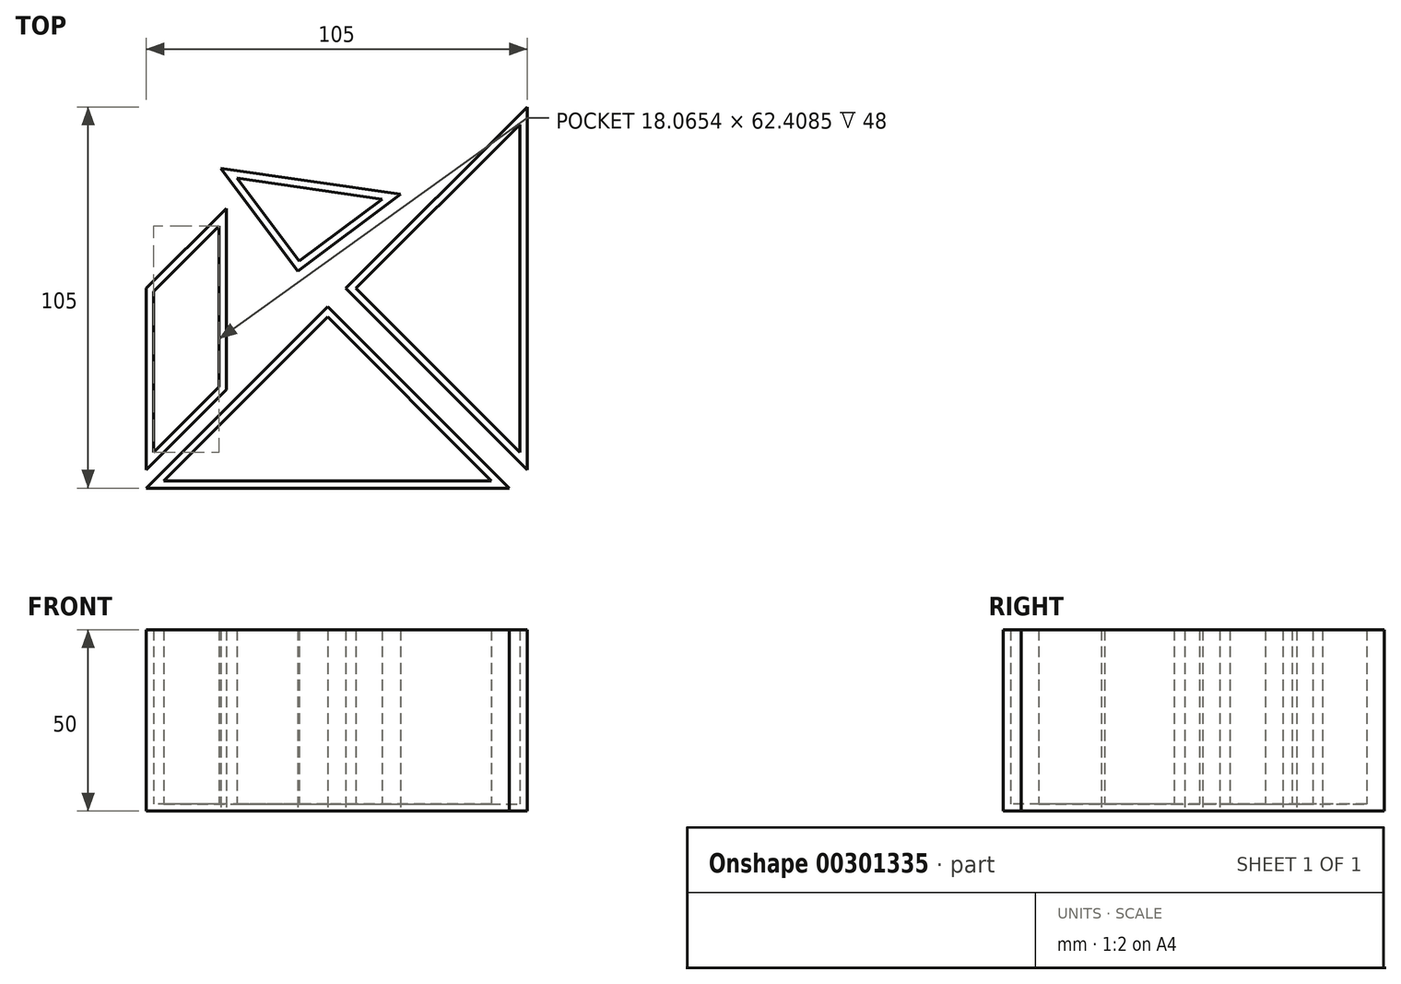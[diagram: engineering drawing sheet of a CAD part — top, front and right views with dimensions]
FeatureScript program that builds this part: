
annotation { "Feature Type Name" : "Feature", "Feature Type Description" : "" }
export const myFeature = defineFeature(function(context is Context, id is Id, definition is map)
    precondition{}
    {
        {
            var Q0;
            Q0=qCreatedBy(makeId("Top.planeOp"),FACE);
            var sketch = newSketch(context, id + "F0", { "sketchPlane" : qUnion([Q0])});
            skLineSegment(sketch, "E0", {"start": v(-121.54, -51.81) * mm, "end": v(-121.54, -101.81) * mm});
            skLineSegment(sketch, "E1", {"start": v(-121.54, -101.81) * mm, "end": v(-99.47, -79.75) * mm});
            skLineSegment(sketch, "E2", {"start": v(-99.47, -79.75) * mm, "end": v(-99.47, -29.75) * mm});
            skLineSegment(sketch, "E3", {"start": v(-99.47, -29.75) * mm, "end": v(-121.54, -51.81) * mm});
            skLineSegment(sketch, "E4", {"start": v(-121.54, -106.81) * mm, "end": v(-21.54, -106.81) * mm});
            skLineSegment(sketch, "E5", {"start": v(-21.54, -106.81) * mm, "end": v(-71.54, -56.81) * mm});
            skLineSegment(sketch, "E6", {"start": v(-71.54, -56.81) * mm, "end": v(-121.54, -106.81) * mm});
            skLineSegment(sketch, "E7", {"start": v(-66.54, -51.81) * mm, "end": v(-16.54, -1.81) * mm});
            skLineSegment(sketch, "E8", {"start": v(-16.54, -1.81) * mm, "end": v(-16.54, -101.81) * mm});
            skLineSegment(sketch, "E9", {"start": v(-16.54, -101.81) * mm, "end": v(-66.54, -51.81) * mm});
            skLineSegment(sketch, "E10", {"start": v(-79.8, -47.08) * mm, "end": v(-100.98, -18.78) * mm});
            skLineSegment(sketch, "E11", {"start": v(-79.8, -47.08) * mm, "end": v(-51.5, -25.9) * mm});
            skLineSegment(sketch, "E12", {"start": v(-100.98, -18.78) * mm, "end": v(-51.5, -25.9) * mm});
            skSolve(sketch);
        }
        {
            var Q0;
            Q0=makeQuery(id+"F0.imprint","IMPRINT",FACE,{"disambiguationData":[TD([[makeQuery(id+"F0.imprint","IMPRINT",EDGE,{"derivedFrom":sQuery(id+"F0.wireOp",EDGE,"gOPFrDLm-Oyjt-phQG-8oZA-UiuvqQgUg0GV")}),-1.0]])]});
            var Q1;
            Q1=makeQuery(id+"F0.imprint","IMPRINT",FACE,{"disambiguationData":[TD([[makeQuery(id+"F0.imprint","IMPRINT",EDGE,{"derivedFrom":sQuery(id+"F0.wireOp",EDGE,"UqGcmN5w-dN8b-6TDN-YQcz-35YnLXxTZRbM")}),-1.0]])]});
            var Q2;
            Q2=makeQuery(id+"F0.imprint","IMPRINT",FACE,{"disambiguationData":[TD([[makeQuery(id+"F0.imprint","IMPRINT",EDGE,{"derivedFrom":sQuery(id+"F0.wireOp",EDGE,"QA9d10xc-AseP-06dk-Ddrk-o75zNBnxM6HC")}),1.0]])]});
            var Q3;
            Q3=makeQuery(id+"F0.imprint","IMPRINT",FACE,{"disambiguationData":[TD([[makeQuery(id+"F0.imprint","IMPRINT",EDGE,{"derivedFrom":sQuery(id+"F0.wireOp",EDGE,"E7")}),-1.0]])]});
            var Q4;
            Q4=makeQuery(id+"F0.imprint","IMPRINT",FACE,{"disambiguationData":[TD([[makeQuery(id+"F0.imprint","IMPRINT",EDGE,{"derivedFrom":sQuery(id+"F0.wireOp",EDGE,"E10")}),-1.0]])]});
            var Q5;
            Q5=makeQuery(id+"F0.imprint","IMPRINT",FACE,{"disambiguationData":[TD([[makeQuery(id+"F0.imprint","IMPRINT",EDGE,{"derivedFrom":sQuery(id+"F0.wireOp",EDGE,"E0")}),1.0]])]});
            var Q6;
            Q6=makeQuery(id+"F0.imprint","IMPRINT",FACE,{"disambiguationData":[TD([[makeQuery(id+"F0.imprint","IMPRINT",EDGE,{"derivedFrom":sQuery(id+"F0.wireOp",EDGE,"E4")}),1.0]])]});
            extrude(context, id + "F1", {"entities" : qUnion([Q0, Q1, Q2, Q3, Q4, Q5, Q6]), "depth" : 50 * mm});
        }
        {
            var Q0;
            Q0=makeQuery(id+"F1.opExtrude","CAP_FACE",FACE,{"disambiguationData":[OSD([sQuery(id+"F0.wireOp",EDGE,"QA9d10xc-AseP-06dk-Ddrk-o75zNBnxM6HC"),sQuery(id+"F0.wireOp",EDGE,"OsFDrU4V-MxnS-ytZD-BNwH-4TMpfRJTvR4B"),sQuery(id+"F0.wireOp",EDGE,"67rH4uF2-G36A-dc7E-XHY2-sjZvzwEkz98M")])],"isStart":false});
            var Q1;
            Q1=makeQuery(id+"F1.opExtrude","CAP_FACE",FACE,{"disambiguationData":[OSD([sQuery(id+"F0.wireOp",EDGE,"UqGcmN5w-dN8b-6TDN-YQcz-35YnLXxTZRbM"),sQuery(id+"F0.wireOp",EDGE,"dNGHm3Kr-Zc99-QYVY-EvTg-v2a4wD3AjYDO"),sQuery(id+"F0.wireOp",EDGE,"blzvPQTa-kEVL-FHaT-gslW-uhKDKKvzhcV0"),sQuery(id+"F0.wireOp",EDGE,"GiMt1YfZ-lZk9-raIQ-PI8C-9DDC4Rn3V4Fj")])],"isStart":false});
            var Q2;
            Q2=makeQuery(id+"F1.opExtrude","CAP_FACE",FACE,{"disambiguationData":[OSD([sQuery(id+"F0.wireOp",EDGE,"E7"),sQuery(id+"F0.wireOp",EDGE,"E8"),sQuery(id+"F0.wireOp",EDGE,"E9")])],"isStart":false});
            var Q3;
            Q3=makeQuery(id+"F1.opExtrude","CAP_FACE",FACE,{"disambiguationData":[OSD([sQuery(id+"F0.wireOp",EDGE,"E4"),sQuery(id+"F0.wireOp",EDGE,"E5"),sQuery(id+"F0.wireOp",EDGE,"E6")])],"isStart":false});
            var Q4;
            Q4=makeQuery(id+"F1.opExtrude","CAP_FACE",FACE,{"disambiguationData":[OSD([sQuery(id+"F0.wireOp",EDGE,"E10"),sQuery(id+"F0.wireOp",EDGE,"E11"),sQuery(id+"F0.wireOp",EDGE,"E12")])],"isStart":false});
            var Q5;
            Q5=makeQuery(id+"F1.opExtrude","CAP_FACE",FACE,{"disambiguationData":[OSD([sQuery(id+"F0.wireOp",EDGE,"E0"),sQuery(id+"F0.wireOp",EDGE,"E1"),sQuery(id+"F0.wireOp",EDGE,"E2"),sQuery(id+"F0.wireOp",EDGE,"E3")])],"isStart":false});
            var Q6;
            Q6=makeQuery(id+"F1.opExtrude","CAP_FACE",FACE,{"disambiguationData":[OSD([sQuery(id+"F0.wireOp",EDGE,"gOPFrDLm-Oyjt-phQG-8oZA-UiuvqQgUg0GV"),sQuery(id+"F0.wireOp",EDGE,"v4gi4XhD-ixuF-12Gm-uLZZ-xqWw5HEaBqZR"),sQuery(id+"F0.wireOp",EDGE,"kOroDRZz-Gujt-XCIK-GF22-nPcpihLVu8FI")])],"isStart":false});
            shell(context, id + "F2", {"entities" : qUnion([Q0, Q1, Q2, Q3, Q4, Q5, Q6]), "thickness" : 2 * mm});
        }
    });
